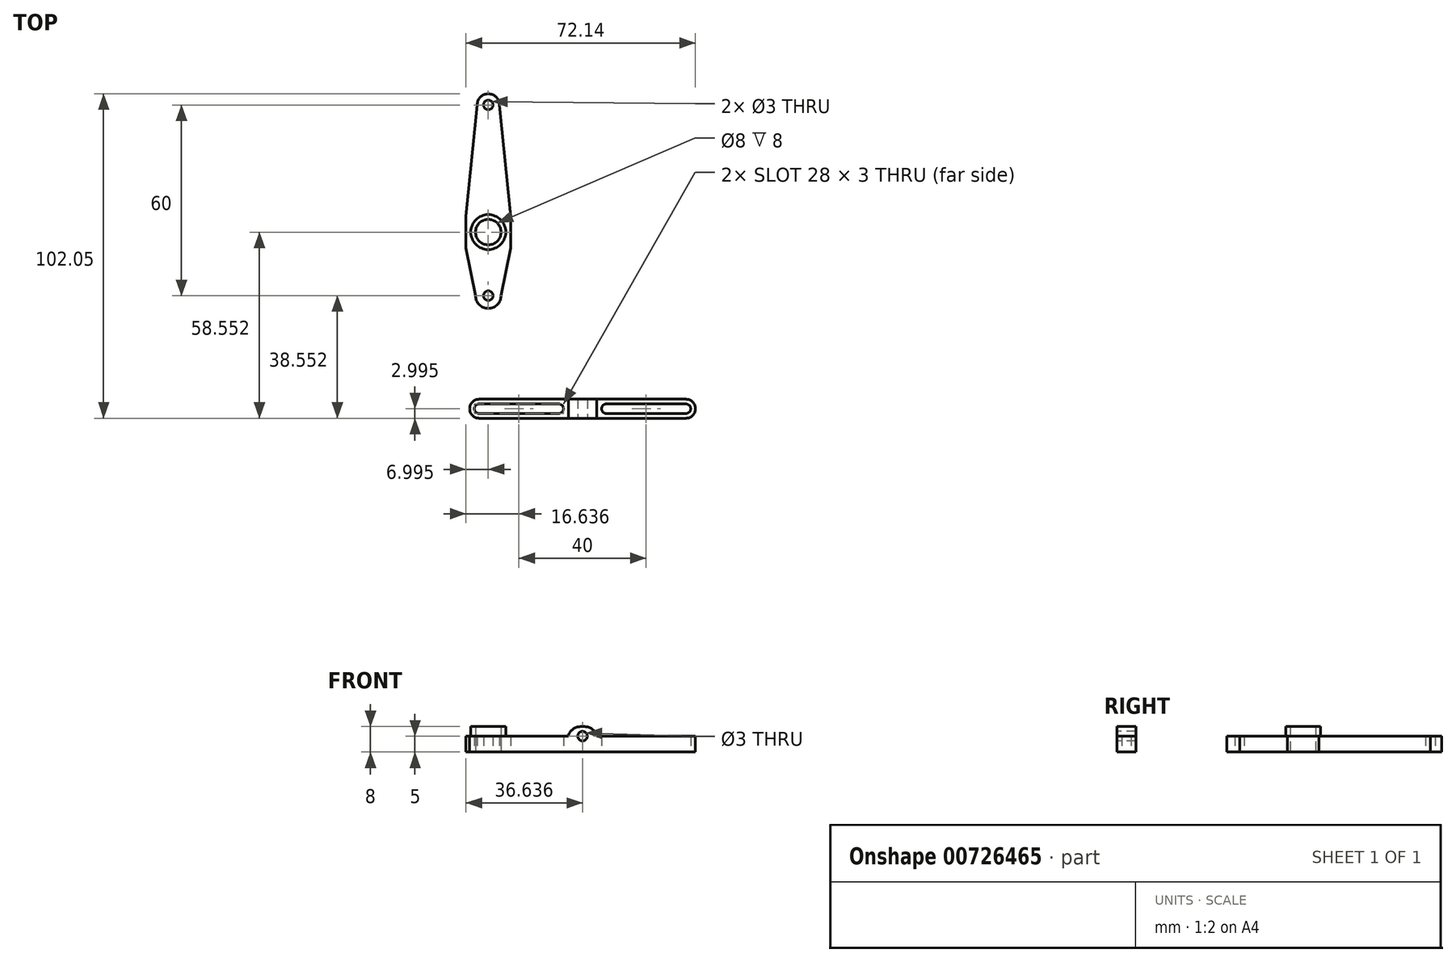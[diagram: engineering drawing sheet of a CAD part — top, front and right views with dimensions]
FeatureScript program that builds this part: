
annotation { "Feature Type Name" : "Feature", "Feature Type Description" : "" }
export const myFeature = defineFeature(function(context is Context, id is Id, definition is map)
    precondition{}
    {
        {
            var Q0;
            Q0=qCreatedBy(makeId("Top.planeOp"),FACE);
            var sketch = newSketch(context, id + "F0", { "sketchPlane" : qUnion([Q0])});
            skCircle(sketch, "E0", {"center": v(-44.04, 19.12) * mm, "radius": 4 * mm});
            skLineSegment(sketch, "E1", {"start": v(-51.04, 24.12) * mm, "end": v(-51.04, 14.12) * mm});
            skLineSegment(sketch, "E2", {"start": v(-37.04, 24.12) * mm, "end": v(-37.04, 14.12) * mm});
            skPoint(sketch, "E3", {"position": v(-37.04, 19.12) * mm});
            skPoint(sketch, "E4", {"position": v(-51.04, 19.12) * mm});
            skLineSegment(sketch, "E5", {"start": v(-44.04, 19.12) * mm, "end": v(-51.04, 19.12) * mm});
            skLineSegment(sketch, "E6", {"start": v(-44.04, 19.12) * mm, "end": v(-37.04, 19.12) * mm});
            skCircle(sketch, "E7", {"center": v(-44.04, 59.12) * mm, "radius": 1.5 * mm});
            skCircle(sketch, "E8", {"center": v(-44.04, -0.88) * mm, "radius": 1.5 * mm});
            skCircle(sketch, "E9", {"center": v(-44.04, -0.88) * mm, "radius": 4 * mm});
            skCircle(sketch, "E10", {"center": v(-44.04, 59.12) * mm, "radius": 3.5 * mm});
            skLineSegment(sketch, "E11", {"start": v(-47.54, 59.12) * mm, "end": v(-51.04, 24.12) * mm});
            skLineSegment(sketch, "E12", {"start": v(-37.04, 24.12) * mm, "end": v(-40.54, 59.12) * mm});
            skLineSegment(sketch, "E13", {"start": v(-51.04, 14.12) * mm, "end": v(-48.04, -0.88) * mm});
            skLineSegment(sketch, "E14", {"start": v(-37.04, 14.12) * mm, "end": v(-40.04, -0.88) * mm});
            skSolve(sketch);
        }
        {
            var Q0;
            {var subQ4=sQuery(id+"F0.wireOp",EDGE,"E11");Q0=makeQuery(id+"F0.imprint","IMPRINT",FACE,{"disambiguationData":[TD([[makeQuery(id+"F0.imprint","IMPRINT",EDGE,{"derivedFrom":subQ4}),1.0]])]});}
            var Q1;
            {var subQ5=sQuery(id+"F0.wireOp",EDGE,"E13");Q1=makeQuery(id+"F0.imprint","IMPRINT",FACE,{"disambiguationData":[TD([[makeQuery(id+"F0.imprint","IMPRINT",EDGE,{"derivedFrom":subQ5}),1.0]])]});}
            var Q2;
            Q2=makeQuery(id+"F0.imprint","IMPRINT",FACE,{"disambiguationData":[TD([[makeQuery(id+"F0.imprint","IMPRINT",EDGE,{"derivedFrom":sQuery(id+"F0.wireOp",EDGE,"E8")}),-1.0]])]});
            var Q3;
            Q3=makeQuery(id+"F0.imprint","IMPRINT",FACE,{"disambiguationData":[TD([[makeQuery(id+"F0.imprint","IMPRINT",EDGE,{"derivedFrom":sQuery(id+"F0.wireOp",EDGE,"E7")}),-1.0]])]});
            extrude(context, id + "F1", {"entities" : qUnion([Q0, Q1, Q2, Q3]), "depth" : 5 * mm, "offsetDistance" : 25 * mm});
        }
        {
            var Q0;
            Q0=makeQuery(id+"F1.opExtrude","CAP_FACE",FACE,{"disambiguationData":[OSD([sQuery(id+"F0.wireOp",EDGE,"E0"),sQuery(id+"F0.wireOp",EDGE,"E1"),sQuery(id+"F0.wireOp",EDGE,"E2"),sQuery(id+"F0.wireOp",EDGE,"E7"),sQuery(id+"F0.wireOp",EDGE,"E8"),sQuery(id+"F0.wireOp",EDGE,"E9"),sQuery(id+"F0.wireOp",EDGE,"E10"),sQuery(id+"F0.wireOp",EDGE,"E11"),sQuery(id+"F0.wireOp",EDGE,"E12"),sQuery(id+"F0.wireOp",EDGE,"E13"),sQuery(id+"F0.wireOp",EDGE,"E14")])],"isStart":false});
            var sketch = newSketch(context, id + "F2", { "sketchPlane" : qUnion([Q0])});
            skCircle(sketch, "E15", {"center": v(-44.04, 19.12) * mm, "radius": 5.5 * mm});
            skSolve(sketch);
        }
        {
            var Q0;
            Q0=makeQuery(id+"F2.imprint","IMPRINT",FACE,{"disambiguationData":[TD([[makeQuery(id+"F2.imprint","IMPRINT",EDGE,{"derivedFrom":sQuery(id+"F2.wireOp",EDGE,"E15")}),1.0]])]});
            extrude(context, id + "F3", {"entities" : qUnion([Q0]), "operationType" : NewBodyOperationType.ADD, "depth" : 3 * mm, "offsetDistance" : 25 * mm});
        }
        {
            var Q0;
            Q0=qCreatedBy(makeId("Top.planeOp"),FACE);
            var sketch = newSketch(context, id + "F4", { "sketchPlane" : qUnion([Q0])});
            skCircle(sketch, "E16", {"center": v(-46.9, -36.43) * mm, "radius": 1.5 * mm});
            skCircle(sketch, "E17", {"center": v(18.1, -36.43) * mm, "radius": 1.5 * mm});
            skCircle(sketch, "E18", {"center": v(-21.9, -36.43) * mm, "radius": 1.5 * mm});
            skCircle(sketch, "E19", {"center": v(-6.9, -36.43) * mm, "radius": 1.5 * mm});
            skLineSegment(sketch, "E20", {"start": v(-46.9, -36.43) * mm, "end": v(-21.9, -36.43) * mm});
            skLineSegment(sketch, "E21", {"start": v(-6.9, -36.43) * mm, "end": v(18.1, -36.43) * mm});
            skLineSegment(sketch, "E22", {"start": v(-21.9, -36.43) * mm, "end": v(-6.9, -36.43) * mm});
            skCircle(sketch, "E23", {"center": v(-46.9, -36.43) * mm, "radius": 3 * mm});
            skCircle(sketch, "E24", {"center": v(18.1, -36.43) * mm, "radius": 3 * mm});
            skLineSegment(sketch, "E25", {"start": v(-46.9, -33.43) * mm, "end": v(18.1, -33.43) * mm});
            skLineSegment(sketch, "E26", {"start": v(-46.9, -39.43) * mm, "end": v(18.1, -39.43) * mm});
            skLineSegment(sketch, "E27", {"start": v(-46.9, -34.93) * mm, "end": v(-21.9, -34.93) * mm});
            skLineSegment(sketch, "E28", {"start": v(-46.9, -37.93) * mm, "end": v(-21.9, -37.93) * mm});
            skLineSegment(sketch, "E29", {"start": v(-6.9, -34.93) * mm, "end": v(18.1, -34.93) * mm});
            skLineSegment(sketch, "E30", {"start": v(-6.9, -37.93) * mm, "end": v(18.1, -37.93) * mm});
            skSolve(sketch);
        }
        {
            var Q0;
            {var subQ0=sQuery(id+"F4.wireOp",EDGE,"E25");Q0=makeQuery(id+"F4.imprint","IMPRINT",FACE,{"disambiguationData":[TD([[makeQuery(id+"F4.imprint","IMPRINT",EDGE,{"derivedFrom":subQ0}),-1.0]])]});}
            var Q1;
            {var subQ0=sQuery(id+"F4.wireOp",EDGE,"E26");Q1=makeQuery(id+"F4.imprint","IMPRINT",FACE,{"disambiguationData":[TD([[makeQuery(id+"F4.imprint","IMPRINT",EDGE,{"derivedFrom":subQ0}),1.0]])]});}
            var Q2;
            {var subQ3=sQuery(id+"F4.wireOp",EDGE,"E27");var subQ5=sQuery(id+"F4.wireOp",EDGE,"E16");var subQ6=makeQuery(id+"F4.imprint","INTERSECT",VERTEX,{"derivedFrom":[subQ5,subQ3]});Q2=makeQuery(id+"F4.imprint","IMPRINT",FACE,{"disambiguationData":[TD([[makeQuery(id+"F4.imprint","IMPRINT",EDGE,{"disambiguationData":[TD([[subQ6,-1.0]])],"derivedFrom":subQ5}),-1.0]])]});}
            var Q3;
            {var subQ5=sQuery(id+"F4.wireOp",EDGE,"E17");var subQ7=sQuery(id+"F4.wireOp",EDGE,"E29");var subQ9=makeQuery(id+"F4.imprint","INTERSECT",VERTEX,{"derivedFrom":[subQ5,subQ7]});Q3=makeQuery(id+"F4.imprint","IMPRINT",FACE,{"disambiguationData":[TD([[makeQuery(id+"F4.imprint","IMPRINT",EDGE,{"disambiguationData":[TD([[subQ9,1.0]])],"derivedFrom":subQ5}),-1.0]])]});}
            extrude(context, id + "F5", {"entities" : qUnion([Q0, Q1, Q2, Q3]), "depth" : 5 * mm, "offsetDistance" : 25 * mm});
        }
        {
            var Q0;
            Q0=makeQuery(id+"F5.opExtrude","CAP_FACE",FACE,{"disambiguationData":[OSD([sQuery(id+"F4.wireOp",EDGE,"E16"),sQuery(id+"F4.wireOp",EDGE,"E17"),sQuery(id+"F4.wireOp",EDGE,"E18"),sQuery(id+"F4.wireOp",EDGE,"E19"),sQuery(id+"F4.wireOp",EDGE,"E23"),sQuery(id+"F4.wireOp",EDGE,"E24"),sQuery(id+"F4.wireOp",EDGE,"E25"),sQuery(id+"F4.wireOp",EDGE,"E26"),sQuery(id+"F4.wireOp",EDGE,"E27"),sQuery(id+"F4.wireOp",EDGE,"E28"),sQuery(id+"F4.wireOp",EDGE,"E29"),sQuery(id+"F4.wireOp",EDGE,"E30")])],"isStart":false});
            var sketch = newSketch(context, id + "F6", { "sketchPlane" : qUnion([Q0])});
            skLineSegment(sketch, "E31.bottom", {"start": v(-18.9, -39.43) * mm, "end": v(-9.9, -39.43) * mm});
            skLineSegment(sketch, "E31.top", {"start": v(-18.9, -33.43) * mm, "end": v(-9.9, -33.43) * mm});
            skLineSegment(sketch, "E31.left", {"start": v(-18.9, -39.43) * mm, "end": v(-18.9, -33.43) * mm});
            skLineSegment(sketch, "E31.right", {"start": v(-9.9, -39.43) * mm, "end": v(-9.9, -33.43) * mm});
            skSolve(sketch);
        }
        {
            var Q0;
            Q0=makeQuery(id+"F6.imprint","IMPRINT",FACE,{"disambiguationData":[TD([[makeQuery(id+"F6.imprint","IMPRINT",EDGE,{"derivedFrom":sQuery(id+"F6.wireOp",EDGE,"E31.bottom")}),1.0]])]});
            extrude(context, id + "F7", {"entities" : qUnion([Q0]), "operationType" : NewBodyOperationType.ADD, "depth" : 3 * mm, "offsetDistance" : 25 * mm});
        }
        {
            var Q0;
            Q0=makeQuery(id+"F7.boolean.opBoolean","MERGE",FACE,{"derivedFrom":[makeQuery(id+"F5.opExtrude","SWEPT_FACE",FACE,{"disambiguationData":[OSD([sQuery(id+"F4.wireOp",EDGE,"E26")])]}),makeQuery(id+"F7.opExtrude","SWEPT_FACE",FACE,{"disambiguationData":[OSD([sQuery(id+"F6.wireOp",EDGE,"E31.bottom")])]})]});
            var sketch = newSketch(context, id + "F8", { "sketchPlane" : qUnion([Q0])});
            skPoint(sketch, "E32", {"position": v(-14.4, 8) * mm});
            skCircle(sketch, "E33", {"center": v(-14.4, 5) * mm, "radius": 1.5 * mm});
            skSolve(sketch);
        }
        {
            var Q0;
            Q0=makeQuery(id+"F8.imprint","IMPRINT",FACE,{"disambiguationData":[TD([[makeQuery(id+"F8.imprint","IMPRINT",EDGE,{"derivedFrom":sQuery(id+"F8.wireOp",EDGE,"E33")}),1.0]])]});
            extrude(context, id + "F9", {"entities" : qUnion([Q0]), "operationType" : NewBodyOperationType.REMOVE, "oppositeDirection" : true, "depth" : 25 * mm, "offsetDistance" : 25 * mm});
        }
        {
            var Q0;
            Q0=makeQuery(id+"F7.opExtrude","CAP_EDGE",EDGE,{"disambiguationData":[OSD([sQuery(id+"F6.wireOp",EDGE,"E31.left")])],"isStart":false});
            var Q1;
            Q1=makeQuery(id+"F7.opExtrude","CAP_EDGE",EDGE,{"disambiguationData":[OSD([sQuery(id+"F6.wireOp",EDGE,"E31.right")])],"isStart":false});
            fillet(context, id + "F10", {"entities" : qUnion([Q0, Q1]), "radius" : 4 * mm, "tangentPropagation" : true, "allowEdgeOverflow" : false});
        }
    });
